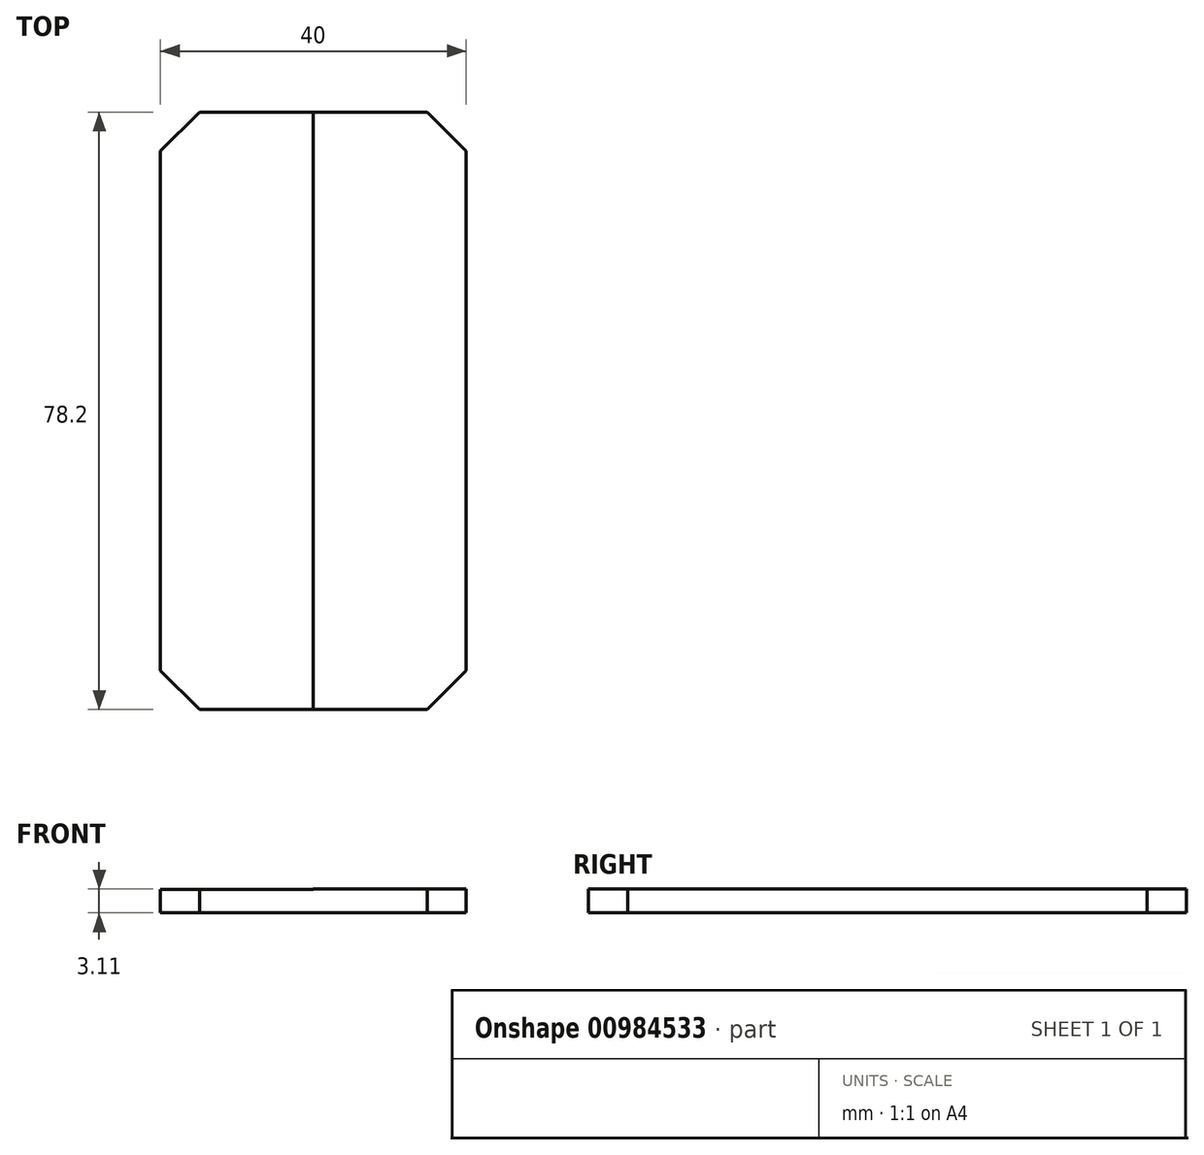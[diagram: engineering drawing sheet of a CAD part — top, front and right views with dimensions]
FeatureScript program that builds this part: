
annotation { "Feature Type Name" : "Feature", "Feature Type Description" : "" }
export const myFeature = defineFeature(function(context is Context, id is Id, definition is map)
    precondition{}
    {
        {
            var Q0;
            Q0=qCreatedBy(makeId("Front.planeOp"),FACE);
            var sketch = newSketch(context, id + "F0", { "sketchPlane" : qUnion([Q0])});
            skLineSegment(sketch, "E0", {"start": v(-20, 0) * mm, "end": v(-20, -3.03) * mm});
            skLineSegment(sketch, "E1", {"start": v(-20, -3.03) * mm, "end": v(20, -3.03) * mm});
            skLineSegment(sketch, "E2", {"start": v(20, -3.03) * mm, "end": v(20, 0.07) * mm});
            skLineSegment(sketch, "E3", {"start": v(20, 0.07) * mm, "end": v(0, 0.07) * mm});
            skLineSegment(sketch, "E4", {"start": v(0, 0.07) * mm, "end": v(0, 0) * mm});
            skLineSegment(sketch, "E5", {"start": v(0, 0) * mm, "end": v(-20, 0) * mm});
            skSolve(sketch);
        }
        {
            var Q0;
            Q0=makeQuery(id+"F0.imprint","IMPRINT",FACE,{"disambiguationData":[TD([[makeQuery(id+"F0.imprint","IMPRINT",EDGE,{"derivedFrom":sQuery(id+"F0.wireOp",EDGE,"E0")}),1.0]])]});
            extrude(context, id + "F1", {"entities" : qUnion([Q0]), "depth" : 78.2 * mm, "offsetDistance" : 25 * mm});
        }
        {
            var Q0;
            Q0=qCreatedBy(makeId("Top.planeOp"),FACE);
            var sketch = newSketch(context, id + "F2", { "sketchPlane" : qUnion([Q0])});
            skLineSegment(sketch, "E6", {"start": v(14.9, 0) * mm, "end": v(20, -5.1) * mm});
            skLineSegment(sketch, "E7", {"start": v(20, -5.1) * mm, "end": v(20, 0) * mm});
            skLineSegment(sketch, "E8", {"start": v(20, 0) * mm, "end": v(14.9, 0) * mm});
            skLineSegment(sketch, "E9", {"start": v(20, -73.1) * mm, "end": v(14.9, -78.2) * mm});
            skLineSegment(sketch, "E10", {"start": v(14.9, -78.2) * mm, "end": v(20, -78.2) * mm});
            skLineSegment(sketch, "E11", {"start": v(20, -78.2) * mm, "end": v(20, -73.1) * mm});
            skLineSegment(sketch, "E12.MirrorCS", {"start": v(-14.9, 0) * mm, "end": v(-20, -5.1) * mm});
            skLineSegment(sketch, "E13.MirrorCS", {"start": v(-20, -73.1) * mm, "end": v(-14.9, -78.2) * mm});
            skLineSegment(sketch, "E14.MirrorCS", {"start": v(-20, -5.1) * mm, "end": v(-20, 0) * mm});
            skLineSegment(sketch, "E15.MirrorCS", {"start": v(-20, 0) * mm, "end": v(-14.9, 0) * mm});
            skLineSegment(sketch, "E16.MirrorCS", {"start": v(-20, -78.2) * mm, "end": v(-20, -73.1) * mm});
            skLineSegment(sketch, "E17.MirrorCS", {"start": v(-14.9, -78.2) * mm, "end": v(-20, -78.2) * mm});
            skSolve(sketch);
        }
        {
            var Q0;
            Q0 = qSketchRegion(id + "F2", true);
            extrude(context, id + "F3", {"entities" : qUnion([Q0]), "operationType" : NewBodyOperationType.REMOVE, "endBound" : BoundingType.SYMMETRIC, "oppositeDirection" : true, "depth" : 10 * mm, "offsetDistance" : 25 * mm});
        }
    });
